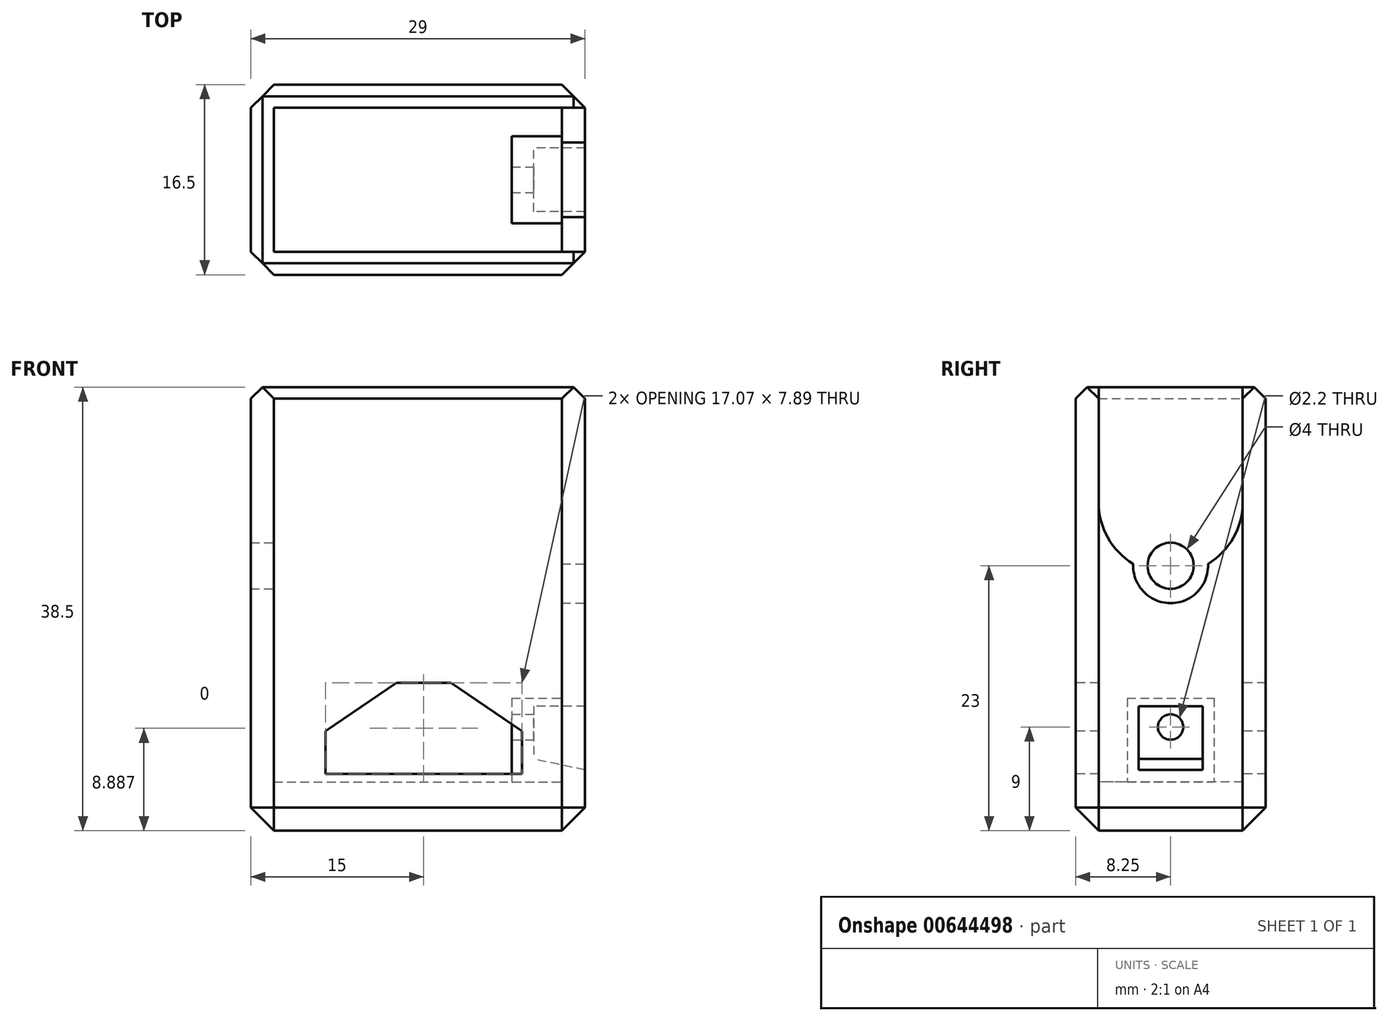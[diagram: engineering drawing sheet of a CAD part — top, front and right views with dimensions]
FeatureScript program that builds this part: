
annotation { "Feature Type Name" : "Feature", "Feature Type Description" : "" }
export const myFeature = defineFeature(function(context is Context, id is Id, definition is map)
    precondition{}
    {
        {
            var Q0;
            Q0=qCreatedBy(makeId("Top.planeOp"),FACE);
            var sketch = newSketch(context, id + "F0", { "sketchPlane" : qUnion([Q0])});
            skLineSegment(sketch, "E0.bottom", {"start": v(0, 16.5) * mm, "end": v(29, 16.5) * mm});
            skLineSegment(sketch, "E0.top", {"start": v(0, 0) * mm, "end": v(29, 0) * mm});
            skLineSegment(sketch, "E0.left", {"start": v(0, 16.5) * mm, "end": v(0, 0) * mm});
            skLineSegment(sketch, "E0.right", {"start": v(29, 16.5) * mm, "end": v(29, 0) * mm});
            skSolve(sketch);
        }
        {
            var Q0;
            Q0=makeQuery(id+"F0.imprint","IMPRINT",FACE,{"disambiguationData":[TD([[makeQuery(id+"F0.imprint","IMPRINT",EDGE,{"derivedFrom":sQuery(id+"F0.wireOp",EDGE,"E0.bottom")}),-1.0]])]});
            extrude(context, id + "F1", {"entities" : qUnion([Q0]), "depth" : 38.5 * mm, "offsetDistance" : 25 * mm});
        }
        {
            var Q0;
            Q0=makeQuery(id+"F1.opExtrude","CAP_FACE",FACE,{"disambiguationData":[OSD([sQuery(id+"F0.wireOp",EDGE,"E0.bottom"),sQuery(id+"F0.wireOp",EDGE,"E0.top"),sQuery(id+"F0.wireOp",EDGE,"E0.left"),sQuery(id+"F0.wireOp",EDGE,"E0.right")])],"isStart":false});
            shell(context, id + "F2", {"entities" : qUnion([Q0]), "thickness" : 2 * mm});
        }
        {
            var Q0;
            Q0=makeQuery(id+"F2.opShell","OFFSET_FACE",FACE,{"disambiguationData":[OSD([sQuery(id+"F0.wireOp",EDGE,"E0.bottom"),sQuery(id+"F0.wireOp",EDGE,"E0.top"),sQuery(id+"F0.wireOp",EDGE,"E0.left"),sQuery(id+"F0.wireOp",EDGE,"E0.right")])]});
            extrude(context, id + "F3", {"entities" : qUnion([Q0]), "operationType" : NewBodyOperationType.ADD, "depth" : 2.25 * mm, "offsetDistance" : 25 * mm});
        }
        {
            var Q0;
            Q0=makeQuery(id+"F1.opExtrude","SWEPT_EDGE",EDGE,{"disambiguationData":[OSD([sQuery(id+"F0.wireOp",EDGE,"E0.bottom"),sQuery(id+"F0.wireOp",EDGE,"E0.left")])]});
            var Q1;
            Q1=makeQuery(id+"F1.opExtrude","SWEPT_EDGE",EDGE,{"disambiguationData":[OSD([sQuery(id+"F0.wireOp",EDGE,"E0.top"),sQuery(id+"F0.wireOp",EDGE,"E0.left")])]});
            var Q2;
            Q2=makeQuery(id+"F1.opExtrude","SWEPT_EDGE",EDGE,{"disambiguationData":[OSD([sQuery(id+"F0.wireOp",EDGE,"E0.bottom"),sQuery(id+"F0.wireOp",EDGE,"E0.right")])]});
            var Q3;
            Q3=makeQuery(id+"F1.opExtrude","SWEPT_EDGE",EDGE,{"disambiguationData":[OSD([sQuery(id+"F0.wireOp",EDGE,"E0.top"),sQuery(id+"F0.wireOp",EDGE,"E0.right")])]});
            var Q4;
            Q4=makeQuery(id+"F1.opExtrude","CAP_EDGE",EDGE,{"disambiguationData":[OSD([sQuery(id+"F0.wireOp",EDGE,"E0.bottom")])],"isStart":true});
            var Q5;
            Q5=makeQuery(id+"F1.opExtrude","CAP_EDGE",EDGE,{"disambiguationData":[OSD([sQuery(id+"F0.wireOp",EDGE,"E0.top")])],"isStart":true});
            var Q6;
            Q6=makeQuery(id+"F1.opExtrude","CAP_EDGE",EDGE,{"disambiguationData":[OSD([sQuery(id+"F0.wireOp",EDGE,"E0.right")])],"isStart":true});
            var Q7;
            Q7=makeQuery(id+"F1.opExtrude","CAP_FACE",FACE,{"disambiguationData":[OSD([sQuery(id+"F0.wireOp",EDGE,"E0.bottom"),sQuery(id+"F0.wireOp",EDGE,"E0.top"),sQuery(id+"F0.wireOp",EDGE,"E0.left"),sQuery(id+"F0.wireOp",EDGE,"E0.right")])],"isStart":true});
            chamfer(context, id + "F4", {"entities" : qUnion([Q0, Q1, Q2, Q3, Q4, Q5, Q6, Q7]), "width" : 2 * mm, "tangentPropagation" : true});
        }
        {
            var Q0;
            Q0=makeQuery(id+"F1.opExtrude","CAP_EDGE",EDGE,{"disambiguationData":[OSD([sQuery(id+"F0.wireOp",EDGE,"E0.bottom")])],"isStart":false});
            var Q1;
            Q1=makeQuery(id+"F1.opExtrude","CAP_EDGE",EDGE,{"disambiguationData":[OSD([sQuery(id+"F0.wireOp",EDGE,"E0.top")])],"isStart":false});
            var Q2;
            Q2=makeQuery(id+"F1.opExtrude","CAP_EDGE",EDGE,{"disambiguationData":[OSD([sQuery(id+"F0.wireOp",EDGE,"E0.left")])],"isStart":false});
            var Q3;
            Q3=makeQuery(id+"F1.opExtrude","CAP_EDGE",EDGE,{"disambiguationData":[OSD([sQuery(id+"F0.wireOp",EDGE,"E0.right")])],"isStart":false});
            chamfer(context, id + "F5", {"entities" : qUnion([Q0, Q1, Q2, Q3]), "width" : 1 * mm, "tangentPropagation" : true});
        }
        {
            var Q0;
            Q0=makeQuery(id+"F1.opExtrude","SWEPT_FACE",FACE,{"disambiguationData":[OSD([sQuery(id+"F0.wireOp",EDGE,"E0.top")])]});
            var sketch = newSketch(context, id + "F6", { "sketchPlane" : qUnion([Q0])});
            skLineSegment(sketch, "E1", {"start": v(6.46, 4.94) * mm, "end": v(23.54, 4.94) * mm});
            skLineSegment(sketch, "E2", {"start": v(23.54, 4.94) * mm, "end": v(23.54, 8.66) * mm});
            skLineSegment(sketch, "E3", {"start": v(23.54, 8.66) * mm, "end": v(17.36, 12.83) * mm});
            skLineSegment(sketch, "E4", {"start": v(17.36, 12.83) * mm, "end": v(12.63, 12.83) * mm});
            skLineSegment(sketch, "E5", {"start": v(12.63, 12.83) * mm, "end": v(6.46, 8.66) * mm});
            skLineSegment(sketch, "E6", {"start": v(6.46, 8.66) * mm, "end": v(6.46, 4.94) * mm});
            skSolve(sketch);
        }
        {
            var Q0;
            Q0=makeQuery(id+"F6.imprint","IMPRINT",FACE,{"disambiguationData":[TD([[makeQuery(id+"F6.imprint","IMPRINT",EDGE,{"derivedFrom":sQuery(id+"F6.wireOp",EDGE,"E1")}),1.0]])]});
            extrude(context, id + "F7", {"entities" : qUnion([Q0]), "operationType" : NewBodyOperationType.REMOVE, "endBound" : BoundingType.THROUGH_ALL, "oppositeDirection" : true, "depth" : 25 * mm, "offsetDistance" : 25 * mm});
        }
        {
            var Q0;
            Q0=makeQuery(id+"F1.opExtrude","SWEPT_FACE",FACE,{"disambiguationData":[OSD([sQuery(id+"F0.wireOp",EDGE,"E0.right")])]});
            var sketch = newSketch(context, id + "F8", { "sketchPlane" : qUnion([Q0])});
            skLineSegment(sketch, "E7.bottom", {"start": v(2, 38.5) * mm, "end": v(14.5, 38.5) * mm});
            skLineSegment(sketch, "E7.top", {"start": v(2, 28.5) * mm, "end": v(14.5, 28.5) * mm});
            skLineSegment(sketch, "E7.left", {"start": v(2, 38.5) * mm, "end": v(2, 28.5) * mm});
            skLineSegment(sketch, "E7.right", {"start": v(14.5, 38.5) * mm, "end": v(14.5, 28.5) * mm});
            skCircle(sketch, "E8", {"center": v(8.25, 28.5) * mm, "radius": 6.25 * mm});
            skCircle(sketch, "E9", {"center": v(8.25, 23) * mm, "radius": 3.25 * mm});
            skSolve(sketch);
        }
        {
            var Q0;
            Q0 = qSketchRegion(id + "F8", true);
            extrude(context, id + "F9", {"entities" : qUnion([Q0]), "operationType" : NewBodyOperationType.REMOVE, "endBound" : BoundingType.UP_TO_NEXT, "oppositeDirection" : true, "depth" : 25 * mm, "offsetDistance" : 25 * mm});
        }
        {
            var Q0;
            Q0=makeQuery(id+"F2.opShell","OFFSET_FACE",FACE,{"disambiguationData":[OSD([sQuery(id+"F0.wireOp",EDGE,"E0.left")])]});
            var sketch = newSketch(context, id + "F10", { "sketchPlane" : qUnion([Q0])});
            skCircle(sketch, "E10", {"center": v(8.25, 23) * mm, "radius": 2 * mm});
            skSolve(sketch);
        }
        {
            var Q0;
            Q0=makeQuery(id+"F10.imprint","IMPRINT",FACE,{"disambiguationData":[TD([[makeQuery(id+"F10.imprint","IMPRINT",EDGE,{"derivedFrom":sQuery(id+"F10.wireOp",EDGE,"E10")}),1.0]])]});
            extrude(context, id + "F11", {"entities" : qUnion([Q0]), "operationType" : NewBodyOperationType.REMOVE, "endBound" : BoundingType.THROUGH_ALL, "oppositeDirection" : true, "depth" : 25 * mm, "offsetDistance" : 25 * mm});
        }
        {
            var Q0;
            Q0=makeQuery(id+"F1.opExtrude","SWEPT_FACE",FACE,{"disambiguationData":[OSD([sQuery(id+"F0.wireOp",EDGE,"E0.right")])]});
            var sketch = newSketch(context, id + "F12", { "sketchPlane" : qUnion([Q0])});
            skLineSegment(sketch, "E11.bottom", {"start": v(4.48, 11.5) * mm, "end": v(12.02, 11.5) * mm});
            skLineSegment(sketch, "E11.top", {"start": v(4.48, 4.25) * mm, "end": v(12.02, 4.25) * mm});
            skLineSegment(sketch, "E11.left", {"start": v(4.48, 11.5) * mm, "end": v(4.48, 4.25) * mm});
            skLineSegment(sketch, "E11.right", {"start": v(12.02, 11.5) * mm, "end": v(12.02, 4.25) * mm});
            skCircle(sketch, "E12", {"center": v(8.25, 9) * mm, "radius": 1.1 * mm});
            skSolve(sketch);
        }
        {
            var Q0;
            Q0=makeQuery(id+"F12.imprint","IMPRINT",FACE,{"disambiguationData":[TD([[makeQuery(id+"F12.imprint","IMPRINT",EDGE,{"derivedFrom":sQuery(id+"F12.wireOp",EDGE,"E11.bottom")}),-1.0]])]});
            extrude(context, id + "F13", {"entities" : qUnion([Q0]), "operationType" : NewBodyOperationType.ADD, "oppositeDirection" : true, "depth" : 6.35 * mm, "offsetDistance" : 25 * mm});
        }
        {
            var Q0;
            Q0=makeQuery(id+"F1.opExtrude","SWEPT_FACE",FACE,{"disambiguationData":[OSD([sQuery(id+"F0.wireOp",EDGE,"E0.right")])]});
            var sketch = newSketch(context, id + "F14", { "sketchPlane" : qUnion([Q0])});
            skLineSegment(sketch, "E13.bottom", {"start": v(5.48, 10.8) * mm, "end": v(11.02, 10.8) * mm});
            skLineSegment(sketch, "E13.top", {"start": v(5.48, 5.27) * mm, "end": v(11.02, 5.27) * mm});
            skLineSegment(sketch, "E13.left", {"start": v(5.48, 10.8) * mm, "end": v(5.48, 5.27) * mm});
            skLineSegment(sketch, "E13.right", {"start": v(11.02, 10.8) * mm, "end": v(11.02, 5.27) * mm});
            skSolve(sketch);
        }
        {
            var Q0;
            Q0=makeQuery(id+"F14.imprint","IMPRINT",FACE,{"disambiguationData":[TD([[makeQuery(id+"F14.imprint","IMPRINT",EDGE,{"derivedFrom":sQuery(id+"F14.wireOp",EDGE,"E13.bottom")}),1.0]])]});
            cPlane(context, id + "F15", {"entities" : qUnion([Q0]), "cplaneType" : CPlaneType.OFFSET, "offset" : 4.45 * mm, "oppositeDirection" : true, "width" : 150 * mm, "height" : 150 * mm});
        }
        {
            var Q0;
            Q0=qCreatedBy(id+"F15.planeOp",FACE);
            var sketch = newSketch(context, id + "F16", { "sketchPlane" : qUnion([Q0])});
            skLineSegment(sketch, "E14.bottom", {"start": v(5.48, 10.8) * mm, "end": v(11.02, 10.8) * mm});
            skLineSegment(sketch, "E14.top", {"start": v(5.48, 6.22) * mm, "end": v(11.02, 6.22) * mm});
            skLineSegment(sketch, "E14.left", {"start": v(5.48, 10.8) * mm, "end": v(5.48, 6.22) * mm});
            skLineSegment(sketch, "E14.right", {"start": v(11.02, 10.8) * mm, "end": v(11.02, 6.22) * mm});
            skSolve(sketch);
        }
        {
            var Q1;
            Q1 = qSketchRegion(id + "F14", true);
            var Q2;
            Q2 = qSketchRegion(id + "F16", true);
            loft(context, id + "F17", {"operationType" : NewBodyOperationType.REMOVE, "sheetProfilesArray" : [{ "sheetProfileEntities" : qUnion([Q1]) }, { "sheetProfileEntities" : qUnion([Q2]) }]});
        }
    });
